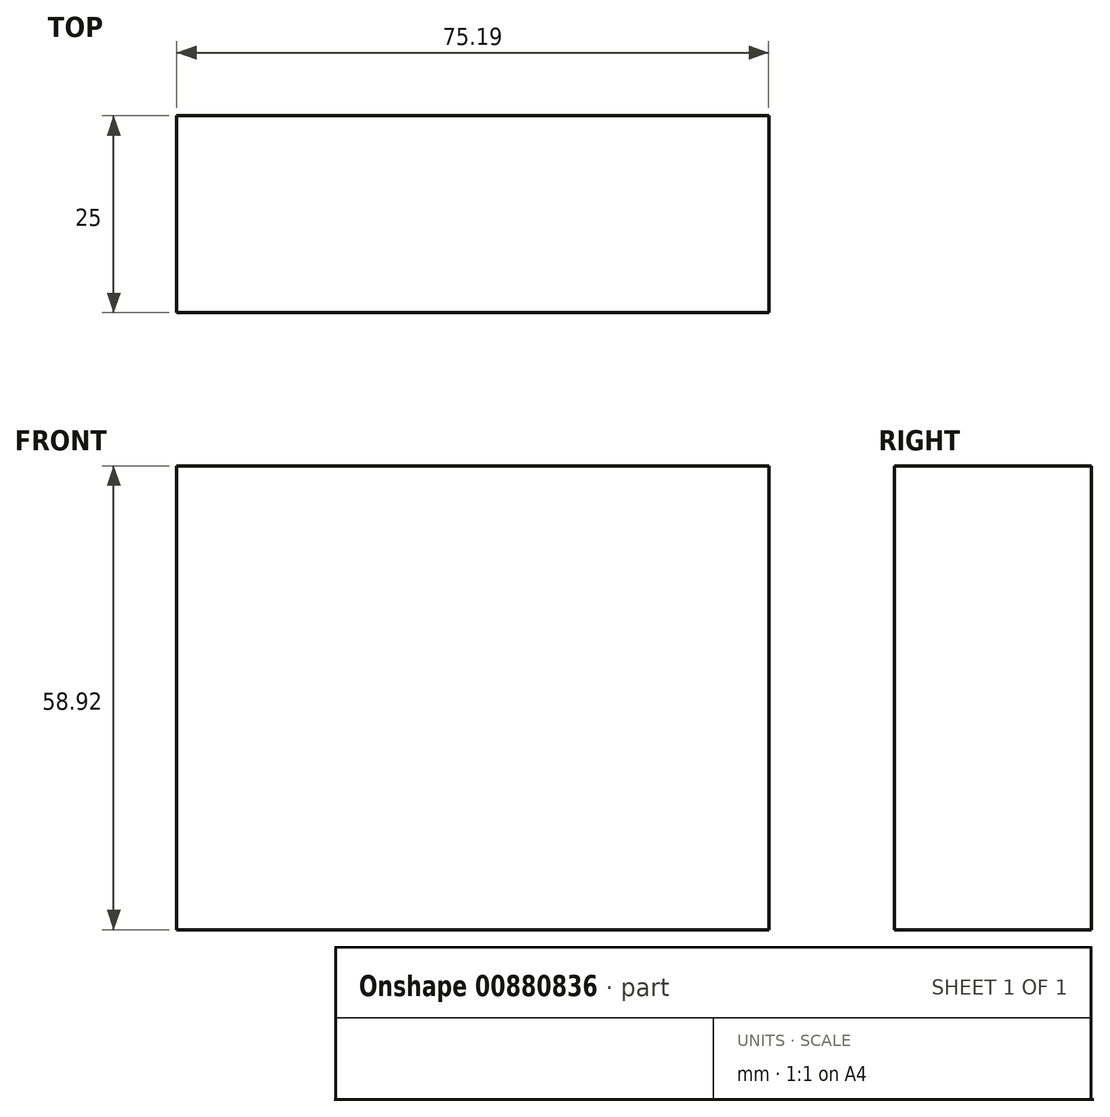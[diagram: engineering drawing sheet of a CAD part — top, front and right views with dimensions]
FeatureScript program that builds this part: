
annotation { "Feature Type Name" : "Feature", "Feature Type Description" : "" }
export const myFeature = defineFeature(function(context is Context, id is Id, definition is map)
    precondition{}
    {
        {
            var Q0;
            Q0=qCreatedBy(makeId("Front.planeOp"),FACE);
            var sketch = newSketch(context, id + "F0", { "sketchPlane" : qUnion([Q0])});
            skLineSegment(sketch, "E0.bottom", {"start": v(-19.98, -21.17) * mm, "end": v(55.21, -21.17) * mm});
            skLineSegment(sketch, "E0.top", {"start": v(-19.98, 37.75) * mm, "end": v(55.21, 37.75) * mm});
            skLineSegment(sketch, "E0.left", {"start": v(-19.98, -21.17) * mm, "end": v(-19.98, 37.75) * mm});
            skLineSegment(sketch, "E0.right", {"start": v(55.21, -21.17) * mm, "end": v(55.21, 37.75) * mm});
            skSolve(sketch);
        }
        {
            var Q0;
            Q0=makeQuery(id+"F0.imprint","IMPRINT",FACE,{"disambiguationData":[TD([[makeQuery(id+"F0.imprint","IMPRINT",EDGE,{"derivedFrom":sQuery(id+"F0.wireOp",EDGE,"E0.bottom")}),1.0]])]});
            extrude(context, id + "F1", {"entities" : qUnion([Q0]), "oppositeDirection" : true, "depth" : 25 * mm, "offsetDistance" : 25 * mm});
        }
    });
